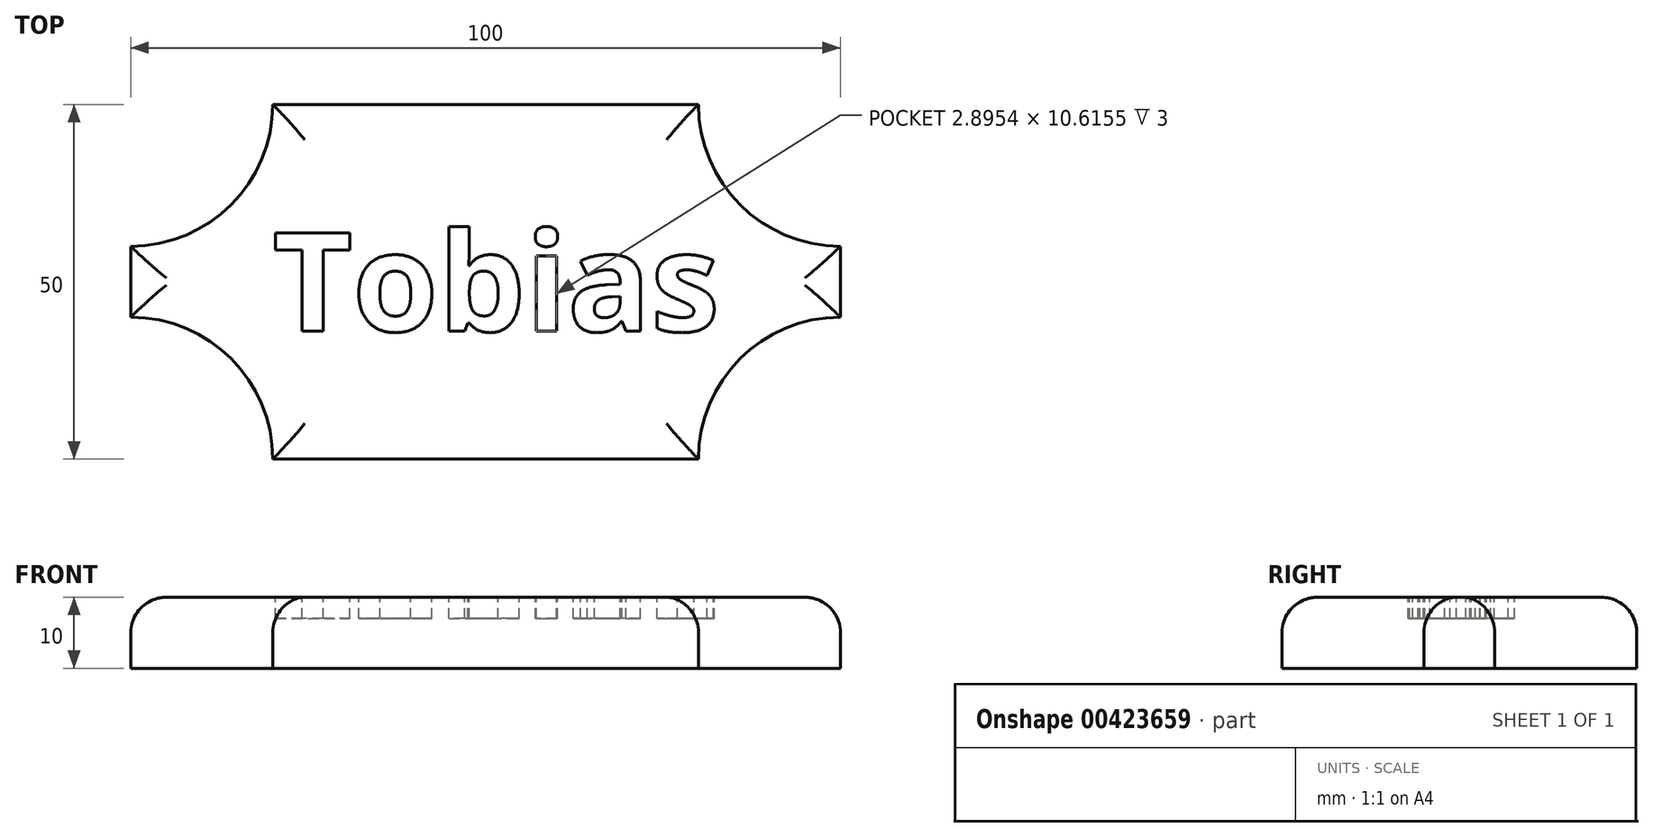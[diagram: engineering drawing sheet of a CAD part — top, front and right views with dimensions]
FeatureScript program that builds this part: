
annotation { "Feature Type Name" : "Feature", "Feature Type Description" : "" }
export const myFeature = defineFeature(function(context is Context, id is Id, definition is map)
    precondition{}
    {
        {
            var Q0;
            Q0=qCreatedBy(makeId("Top.planeOp"),FACE);
            var sketch = newSketch(context, id + "F0", { "sketchPlane" : qUnion([Q0])});
            skLineSegment(sketch, "E0.bottom", {"start": v(0, 0) * mm, "end": v(80, 0) * mm});
            skLineSegment(sketch, "E0.top", {"start": v(20, 50) * mm, "end": v(80, 50) * mm});
            skLineSegment(sketch, "E0.left", {"start": v(0, 20) * mm, "end": v(0, 30) * mm});
            skLineSegment(sketch, "E0.right", {"start": v(100, 0) * mm, "end": v(100, 30) * mm});
            skArc(sketch, "E1", {"start": v(20, 0) * mm, "mid": v(14.14, 14.14) * mm, "end": v(0, 20) * mm});
            skArc(sketch, "E2", {"start": v(0, 30) * mm, "mid": v(14.14, 35.86) * mm, "end": v(20, 50) * mm});
            skArc(sketch, "E3", {"start": v(100, 30) * mm, "mid": v(85.86, 35.86) * mm, "end": v(80, 50) * mm});
            skArc(sketch, "E4", {"start": v(100, 20) * mm, "mid": v(85.86, 14.14) * mm, "end": v(80, 0) * mm});
            skSolve(sketch);
        }
        {
            var Q0;
            Q0 = qSketchRegion(id + "F0", true);
            extrude(context, id + "F1", {"entities" : qUnion([Q0]), "depth" : 10 * mm});
        }
        {
            var Q0;
            Q0=makeQuery(id+"F1.opExtrude","CAP_EDGE",EDGE,{"disambiguationData":[OSD([sQuery(id+"F0.wireOp",EDGE,"E0.bottom")])],"isStart":false});
            var Q1;
            Q1=makeQuery(id+"F1.opExtrude","CAP_EDGE",EDGE,{"disambiguationData":[OSD([sQuery(id+"F0.wireOp",EDGE,"E1")])],"isStart":false});
            var Q2;
            Q2=makeQuery(id+"F1.opExtrude","CAP_EDGE",EDGE,{"disambiguationData":[OSD([sQuery(id+"F0.wireOp",EDGE,"E0.left")])],"isStart":false});
            var Q3;
            Q3=makeQuery(id+"F1.opExtrude","CAP_EDGE",EDGE,{"disambiguationData":[OSD([sQuery(id+"F0.wireOp",EDGE,"E2")])],"isStart":false});
            var Q4;
            Q4=makeQuery(id+"F1.opExtrude","CAP_EDGE",EDGE,{"disambiguationData":[OSD([sQuery(id+"F0.wireOp",EDGE,"E0.top")])],"isStart":false});
            var Q5;
            Q5=makeQuery(id+"F1.opExtrude","CAP_EDGE",EDGE,{"disambiguationData":[OSD([sQuery(id+"F0.wireOp",EDGE,"E3")])],"isStart":false});
            var Q6;
            Q6=makeQuery(id+"F1.opExtrude","CAP_EDGE",EDGE,{"disambiguationData":[OSD([sQuery(id+"F0.wireOp",EDGE,"E4")])],"isStart":false});
            var Q7;
            Q7=makeQuery(id+"F1.opExtrude","CAP_EDGE",EDGE,{"disambiguationData":[OSD([sQuery(id+"F0.wireOp",EDGE,"E0.right")])],"isStart":false});
            fillet(context, id + "F2", {"entities" : qUnion([Q0, Q1, Q2, Q3, Q4, Q5, Q6, Q7]), "radius" : 5 * mm, "tangentPropagation" : true, "allowEdgeOverflow" : false});
        }
        {
            var Q0;
            Q0=makeQuery(id+"F1.opExtrude","CAP_FACE",FACE,{"disambiguationData":[OSD([sQuery(id+"F0.wireOp",EDGE,"E0.bottom"),sQuery(id+"F0.wireOp",EDGE,"E0.top"),sQuery(id+"F0.wireOp",EDGE,"E0.left"),sQuery(id+"F0.wireOp",EDGE,"E0.right"),sQuery(id+"F0.wireOp",EDGE,"E1"),sQuery(id+"F0.wireOp",EDGE,"E2"),sQuery(id+"F0.wireOp",EDGE,"E3"),sQuery(id+"F0.wireOp",EDGE,"E4")])],"isStart":false});
            var sketch = newSketch(context, id + "F3", { "sketchPlane" : qUnion([Q0])});
            skLineSegment(sketch, "E5", {"start": v(5, 25) * mm, "end": v(20, 25) * mm, "construction": true});
            skLineSegment(sketch, "E6", {"start": v(20, 25) * mm, "end": v(20, 32) * mm, "construction": true});
            skText(sketch, "E7", { "text": "Tobias", "fontName": "OpenSans-Bold.ttf"});
            const initialGuessF3  = {"E7": [0.02, 0.018, 1, 0, 0.014]};
            skSetInitialGuess(sketch, initialGuessF3);
            skSolve(sketch);
        }
        {
            var Q0;
            Q0 = qSketchRegion(id + "F3", true);
            extrude(context, id + "F4", {"entities" : qUnion([Q0]), "operationType" : NewBodyOperationType.REMOVE, "oppositeDirection" : true, "depth" : 3 * mm});
        }
    });
